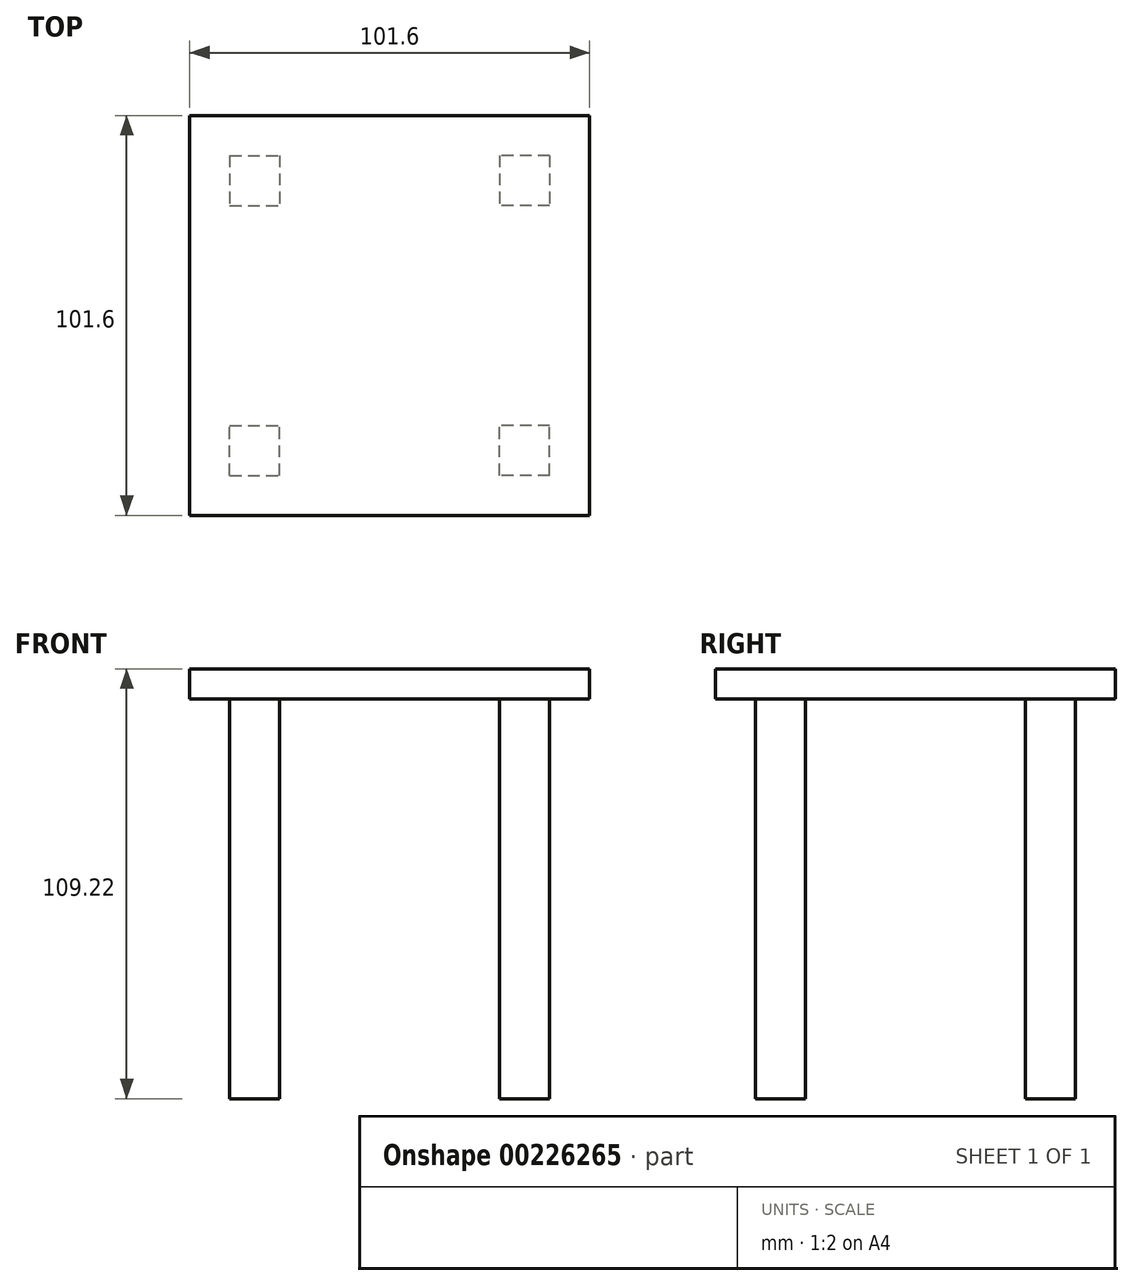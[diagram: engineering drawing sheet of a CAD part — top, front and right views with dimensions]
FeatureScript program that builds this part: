
annotation { "Feature Type Name" : "Feature", "Feature Type Description" : "" }
export const myFeature = defineFeature(function(context is Context, id is Id, definition is map)
    precondition{}
    {
        {
            var Q0;
            Q0=qCreatedBy(makeId("Top.planeOp"),FACE);
            var sketch = newSketch(context, id + "F0", { "sketchPlane" : qUnion([Q0])});
            skLineSegment(sketch, "E0.bottom", {"start": v(-50.8, -50.8) * mm, "end": v(50.8, -50.8) * mm});
            skLineSegment(sketch, "E0.top", {"start": v(-50.8, 50.8) * mm, "end": v(50.8, 50.8) * mm});
            skLineSegment(sketch, "E0.left", {"start": v(-50.8, -50.8) * mm, "end": v(-50.8, 50.8) * mm});
            skLineSegment(sketch, "E0.right", {"start": v(50.8, -50.8) * mm, "end": v(50.8, 50.8) * mm});
            skPoint(sketch, "E0.middle", {"position": v(0, 0) * mm});
            skSolve(sketch);
        }
        {
            var Q0;
            Q0=makeQuery(id+"F0.imprint","IMPRINT",FACE,{"disambiguationData":[TD([[makeQuery(id+"F0.imprint","IMPRINT",EDGE,{"derivedFrom":sQuery(id+"F0.wireOp",EDGE,"E0.bottom")}),1.0]])]});
            extrude(context, id + "F1", {"entities" : qUnion([Q0]), "depth" : 7.62 * mm});
        }
        {
            var Q0;
            Q0=makeQuery(id+"F1.opExtrude","CAP_FACE",FACE,{"disambiguationData":[OSD([sQuery(id+"F0.wireOp",EDGE,"E0.bottom"),sQuery(id+"F0.wireOp",EDGE,"E0.top"),sQuery(id+"F0.wireOp",EDGE,"E0.left"),sQuery(id+"F0.wireOp",EDGE,"E0.right")])],"isStart":true});
            var sketch = newSketch(context, id + "F2", { "sketchPlane" : qUnion([Q0])});
            skLineSegment(sketch, "E1.bottom", {"start": v(-40.64, 40.64) * mm, "end": v(-27.94, 40.64) * mm});
            skLineSegment(sketch, "E1.top", {"start": v(-40.64, 27.94) * mm, "end": v(-27.94, 27.94) * mm});
            skLineSegment(sketch, "E1.left", {"start": v(-40.64, 40.64) * mm, "end": v(-40.64, 27.94) * mm});
            skLineSegment(sketch, "E1.right", {"start": v(-27.94, 40.64) * mm, "end": v(-27.94, 27.94) * mm});
            skLineSegment(sketch, "E2.MirrorCS", {"start": v(40.64, 27.94) * mm, "end": v(27.94, 27.94) * mm});
            skLineSegment(sketch, "E3.MirrorCS", {"start": v(27.94, 40.64) * mm, "end": v(27.94, 27.94) * mm});
            skLineSegment(sketch, "E4.MirrorCS", {"start": v(40.64, 40.64) * mm, "end": v(27.94, 40.64) * mm});
            skLineSegment(sketch, "E5.MirrorCS", {"start": v(40.64, 40.64) * mm, "end": v(40.64, 27.94) * mm});
            skLineSegment(sketch, "E6.MirrorCS", {"start": v(40.64, -27.94) * mm, "end": v(27.94, -27.94) * mm});
            skLineSegment(sketch, "E7.MirrorCS", {"start": v(40.64, -40.64) * mm, "end": v(27.94, -40.64) * mm});
            skLineSegment(sketch, "E8.MirrorCS", {"start": v(40.64, -40.64) * mm, "end": v(40.64, -27.94) * mm});
            skLineSegment(sketch, "E9.MirrorCS", {"start": v(27.94, -40.64) * mm, "end": v(27.94, -27.94) * mm});
            skLineSegment(sketch, "E10.MirrorCS", {"start": v(-40.64, -27.94) * mm, "end": v(-27.94, -27.94) * mm});
            skLineSegment(sketch, "E11.MirrorCS", {"start": v(-40.64, -40.64) * mm, "end": v(-40.64, -27.94) * mm});
            skLineSegment(sketch, "E12.MirrorCS", {"start": v(-40.64, -40.64) * mm, "end": v(-27.94, -40.64) * mm});
            skLineSegment(sketch, "E13.MirrorCS", {"start": v(-27.94, -40.64) * mm, "end": v(-27.94, -27.94) * mm});
            skSolve(sketch);
        }
        {
            var Q0;
            Q0=makeQuery(id+"F2.imprint","IMPRINT",FACE,{"disambiguationData":[TD([[makeQuery(id+"F2.imprint","IMPRINT",EDGE,{"derivedFrom":sQuery(id+"F2.wireOp",EDGE,"E2.MirrorCS")}),-1.0]])]});
            var Q1;
            Q1=makeQuery(id+"F2.imprint","IMPRINT",FACE,{"disambiguationData":[TD([[makeQuery(id+"F2.imprint","IMPRINT",EDGE,{"derivedFrom":sQuery(id+"F2.wireOp",EDGE,"E6.MirrorCS")}),1.0]])]});
            var Q2;
            Q2=makeQuery(id+"F2.imprint","IMPRINT",FACE,{"disambiguationData":[TD([[makeQuery(id+"F2.imprint","IMPRINT",EDGE,{"derivedFrom":sQuery(id+"F2.wireOp",EDGE,"E10.MirrorCS")}),-1.0]])]});
            var Q3;
            Q3=makeQuery(id+"F2.imprint","IMPRINT",FACE,{"disambiguationData":[TD([[makeQuery(id+"F2.imprint","IMPRINT",EDGE,{"derivedFrom":sQuery(id+"F2.wireOp",EDGE,"E1.bottom")}),-1.0]])]});
            extrude(context, id + "F3", {"entities" : qUnion([Q0, Q1, Q2, Q3]), "operationType" : NewBodyOperationType.ADD, "depth" : 101.6 * mm});
        }
    });
